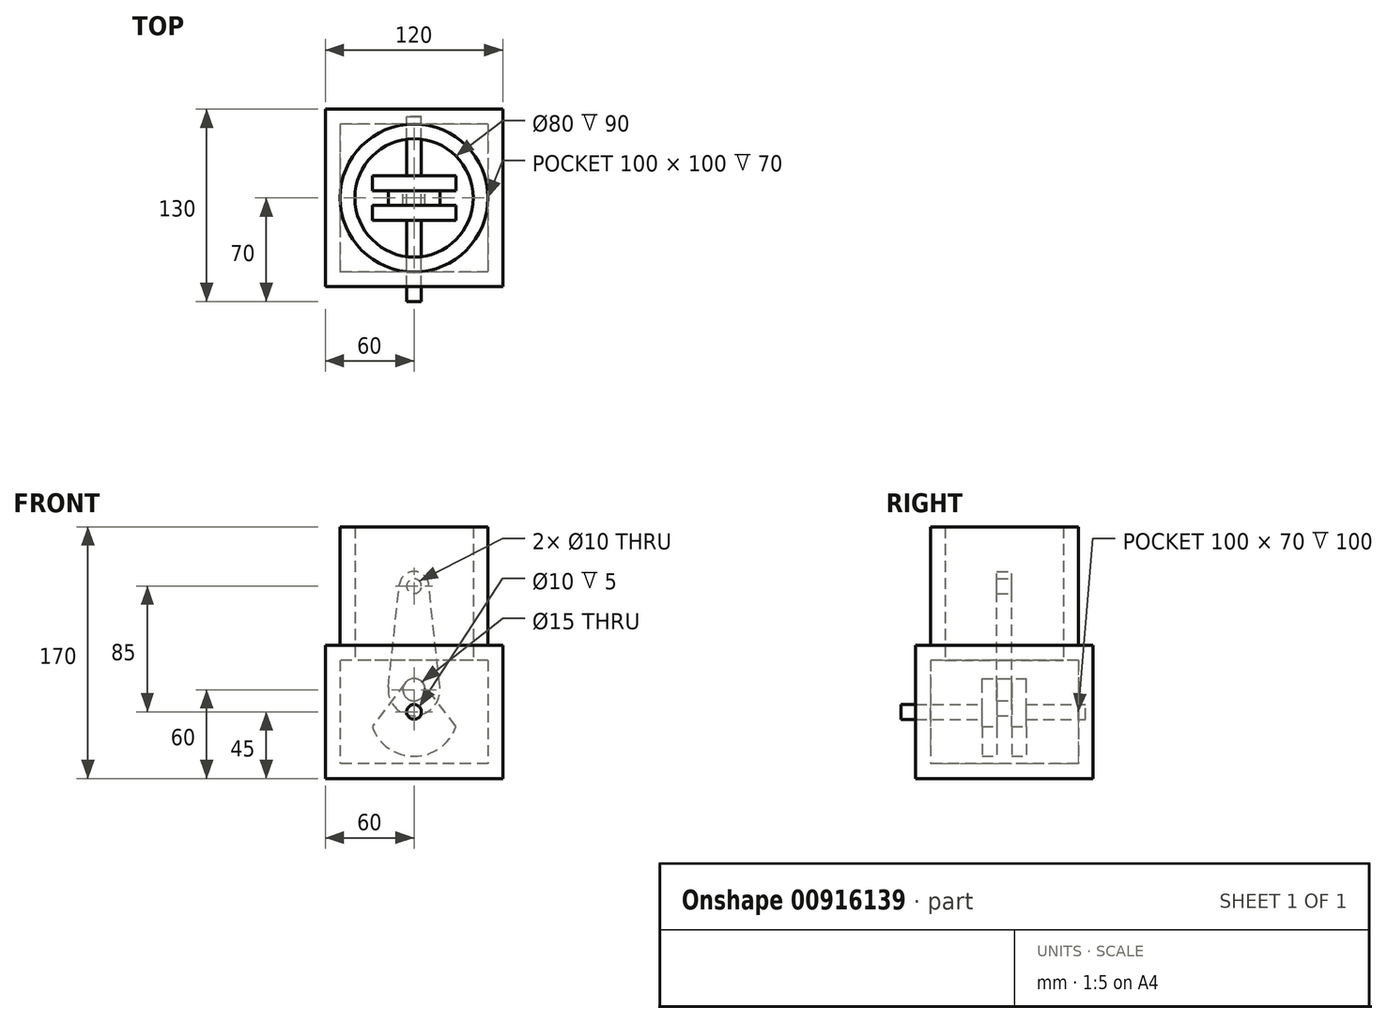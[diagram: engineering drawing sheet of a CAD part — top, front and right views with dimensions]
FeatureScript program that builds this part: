
annotation { "Feature Type Name" : "Feature", "Feature Type Description" : "" }
export const myFeature = defineFeature(function(context is Context, id is Id, definition is map)
    precondition{}
    {
        {
            var Q0;
            Q0=qCreatedBy(makeId("Top.planeOp"),FACE);
            var sketch = newSketch(context, id + "F0", { "sketchPlane" : qUnion([Q0])});
            skLineSegment(sketch, "E0.bottom", {"start": v(60, 60) * mm, "end": v(-60, 60) * mm});
            skLineSegment(sketch, "E0.top", {"start": v(60, -60) * mm, "end": v(-60, -60) * mm});
            skLineSegment(sketch, "E0.left", {"start": v(60, 60) * mm, "end": v(60, -60) * mm});
            skLineSegment(sketch, "E0.right", {"start": v(-60, 60) * mm, "end": v(-60, -60) * mm});
            skPoint(sketch, "E0.middle", {"position": v(0, 0) * mm});
            skSolve(sketch);
        }
        {
            var Q0;
            Q0 = qSketchRegion(id + "F0", true);
            extrude(context, id + "F1", {"entities" : qUnion([Q0]), "depth" : 80 * mm, "offsetDistance" : 25 * mm});
        }
        {
            var Q0;
            Q0=makeQuery(id+"F1.opExtrude","CAP_FACE",FACE,{"disambiguationData":[OSD([sQuery(id+"F0.wireOp",EDGE,"E0.bottom"),sQuery(id+"F0.wireOp",EDGE,"E0.top"),sQuery(id+"F0.wireOp",EDGE,"E0.left"),sQuery(id+"F0.wireOp",EDGE,"E0.right")])],"isStart":false});
            shell(context, id + "F2", {"entities" : qUnion([Q0]), "thickness" : 10 * mm});
        }
        {
            var Q0;
            Q0=qCreatedBy(makeId("Front.planeOp"),FACE);
            var sketch = newSketch(context, id + "F3", { "sketchPlane" : qUnion([Q0])});
            skCircle(sketch, "E1", {"center": v(0, 45) * mm, "radius": 5 * mm});
            skSolve(sketch);
        }
        {
            var Q0;
            Q0 = qSketchRegion(id + "F3", true);
            extrude(context, id + "F4", {"entities" : qUnion([Q0]), "depth" : 70 * mm, "offsetDistance" : 25 * mm, "hasSecondDirection" : true, "secondDirectionOppositeDirection" : true, "secondDirectionDepth" : 55 * mm});
        }
        {
            var Q0;
            Q0=makeQuery(id+"F4.opExtrude","SWEPT_BODY",BODY,{"disambiguationData":[OSD([sQuery(id+"F3.wireOp",EDGE,"E1")])]});
            var Q1;
            Q1=makeQuery(id+"F1.opExtrude","SWEPT_BODY",BODY,{"disambiguationData":[OSD([sQuery(id+"F0.wireOp",EDGE,"E0.bottom"),sQuery(id+"F0.wireOp",EDGE,"E0.top"),sQuery(id+"F0.wireOp",EDGE,"E0.left"),sQuery(id+"F0.wireOp",EDGE,"E0.right")])]});
            booleanBodies(context, id + "F5", {"operationType" : BooleanOperationType.SUBTRACTION, "tools" : qUnion([Q0]), "targets" : qUnion([Q1]), "keepTools" : true});
        }
        {
            var Q0;
            Q0=qCreatedBy(makeId("Front.planeOp"),FACE);
            var sketch = newSketch(context, id + "F6", { "sketchPlane" : qUnion([Q0])});
            skArc(sketch, "E2", {"start": v(-28.28, 35) * mm, "mid": v(0, 15) * mm, "end": v(28.28, 35) * mm});
            skCircle(sketch, "E3", {"center": v(0, 60) * mm, "radius": 7.5 * mm});
            skLineSegment(sketch, "E4", {"start": v(28.28, 35) * mm, "end": v(5.98, 64.52) * mm});
            skLineSegment(sketch, "E5.MirrorCS", {"start": v(-28.28, 35) * mm, "end": v(-5.98, 64.52) * mm});
            skSolve(sketch);
        }
        {
            var Q0;
            Q0 = qSketchRegion(id + "F6", true);
            extrude(context, id + "F7", {"entities" : qUnion([Q0]), "operationType" : NewBodyOperationType.ADD, "endBound" : BoundingType.SYMMETRIC, "depth" : 30 * mm, "offsetDistance" : 25 * mm});
        }
        {
            var Q0;
            Q0=qCreatedBy(makeId("Front.planeOp"),FACE);
            var sketch = newSketch(context, id + "F8", { "sketchPlane" : qUnion([Q0])});
            skLineSegment(sketch, "E6.0.0", {"start": v(28.28, 35) * mm, "end": v(5.98, 64.52) * mm});
            skLineSegment(sketch, "E6.0.2", {"start": v(-5.98, 64.52) * mm, "end": v(-28.28, 35) * mm});
            skArc(sketch, "E6.0.3", {"start": v(-28.28, 35) * mm, "mid": v(0, 15) * mm, "end": v(28.28, 35) * mm});
            skArc(sketch, "E7", {"start": v(-5.98, 64.52) * mm, "mid": v(0, 52.5) * mm, "end": v(5.98, 64.52) * mm});
            skSolve(sketch);
        }
        {
            var Q0;
            Q0 = qSketchRegion(id + "F8", true);
            extrude(context, id + "F9", {"entities" : qUnion([Q0]), "operationType" : NewBodyOperationType.REMOVE, "endBound" : BoundingType.SYMMETRIC, "depth" : 10 * mm, "offsetDistance" : 25 * mm});
        }
        {
            var Q0;
            Q0=qCreatedBy(makeId("Front.planeOp"),FACE);
            var sketch = newSketch(context, id + "F10", { "sketchPlane" : qUnion([Q0])});
            skArc(sketch, "E8.0", {"start": v(5.98, 64.52) * mm, "mid": v(0, 67.5) * mm, "end": v(-5.98, 64.52) * mm});
            skArc(sketch, "E9.0", {"start": v(-5.98, 64.52) * mm, "mid": v(0, 52.5) * mm, "end": v(5.98, 64.52) * mm});
            skCircle(sketch, "E10", {"center": v(0, 60) * mm, "radius": 17.5 * mm});
            skCircle(sketch, "E11", {"center": v(0, 130) * mm, "radius": 5 * mm});
            skCircle(sketch, "E12", {"center": v(0, 130) * mm, "radius": 10 * mm});
            skLineSegment(sketch, "E13", {"start": v(17.4, 61.87) * mm, "end": v(9.94, 131.07) * mm});
            skLineSegment(sketch, "E14.MirrorCS", {"start": v(-17.4, 61.87) * mm, "end": v(-9.94, 131.07) * mm});
            skSolve(sketch);
        }
        {
            var Q0;
            Q0 = qSketchRegion(id + "F10", true);
            extrude(context, id + "F11", {"entities" : qUnion([Q0]), "endBound" : BoundingType.SYMMETRIC, "depth" : 10 * mm, "offsetDistance" : 25 * mm});
        }
        {
            var Q0;
            Q0=makeQuery(id+"F1.opExtrude","CAP_FACE",FACE,{"disambiguationData":[OSD([sQuery(id+"F0.wireOp",EDGE,"E0.bottom"),sQuery(id+"F0.wireOp",EDGE,"E0.top"),sQuery(id+"F0.wireOp",EDGE,"E0.left"),sQuery(id+"F0.wireOp",EDGE,"E0.right")])],"isStart":false});
            var sketch = newSketch(context, id + "F12", { "sketchPlane" : qUnion([Q0])});
            skCircle(sketch, "E15", {"center": v(0, 0) * mm, "radius": 40 * mm});
            skLineSegment(sketch, "E16.bottom", {"start": v(-60, 60) * mm, "end": v(60, 60) * mm});
            skLineSegment(sketch, "E16.top", {"start": v(-60, -60) * mm, "end": v(60, -60) * mm});
            skLineSegment(sketch, "E16.left", {"start": v(-60, 60) * mm, "end": v(-60, -60) * mm});
            skLineSegment(sketch, "E16.right", {"start": v(60, 60) * mm, "end": v(60, -60) * mm});
            skSolve(sketch);
        }
        {
            var Q0;
            Q0 = qSketchRegion(id + "F12", true);
            extrude(context, id + "F13", {"entities" : qUnion([Q0]), "operationType" : NewBodyOperationType.ADD, "depth" : 10 * mm, "offsetDistance" : 25 * mm});
        }
        {
            var Q0;
            Q0=makeQuery(id+"F13.opExtrude","CAP_FACE",FACE,{"disambiguationData":[OSD([sQuery(id+"F12.wireOp",EDGE,"E15"),sQuery(id+"F12.wireOp",EDGE,"E16.bottom"),sQuery(id+"F12.wireOp",EDGE,"E16.top"),sQuery(id+"F12.wireOp",EDGE,"E16.left"),sQuery(id+"F12.wireOp",EDGE,"E16.right")])],"isStart":false});
            var sketch = newSketch(context, id + "F14", { "sketchPlane" : qUnion([Q0])});
            skCircle(sketch, "E17.0", {"center": v(0, 0) * mm, "radius": 40 * mm});
            skCircle(sketch, "E18", {"center": v(0, 0) * mm, "radius": 50 * mm});
            skSolve(sketch);
        }
        {
            var Q0;
            Q0 = qSketchRegion(id + "F14", true);
            extrude(context, id + "F15", {"entities" : qUnion([Q0]), "operationType" : NewBodyOperationType.ADD, "depth" : 80 * mm, "offsetDistance" : 25 * mm});
        }
    });
